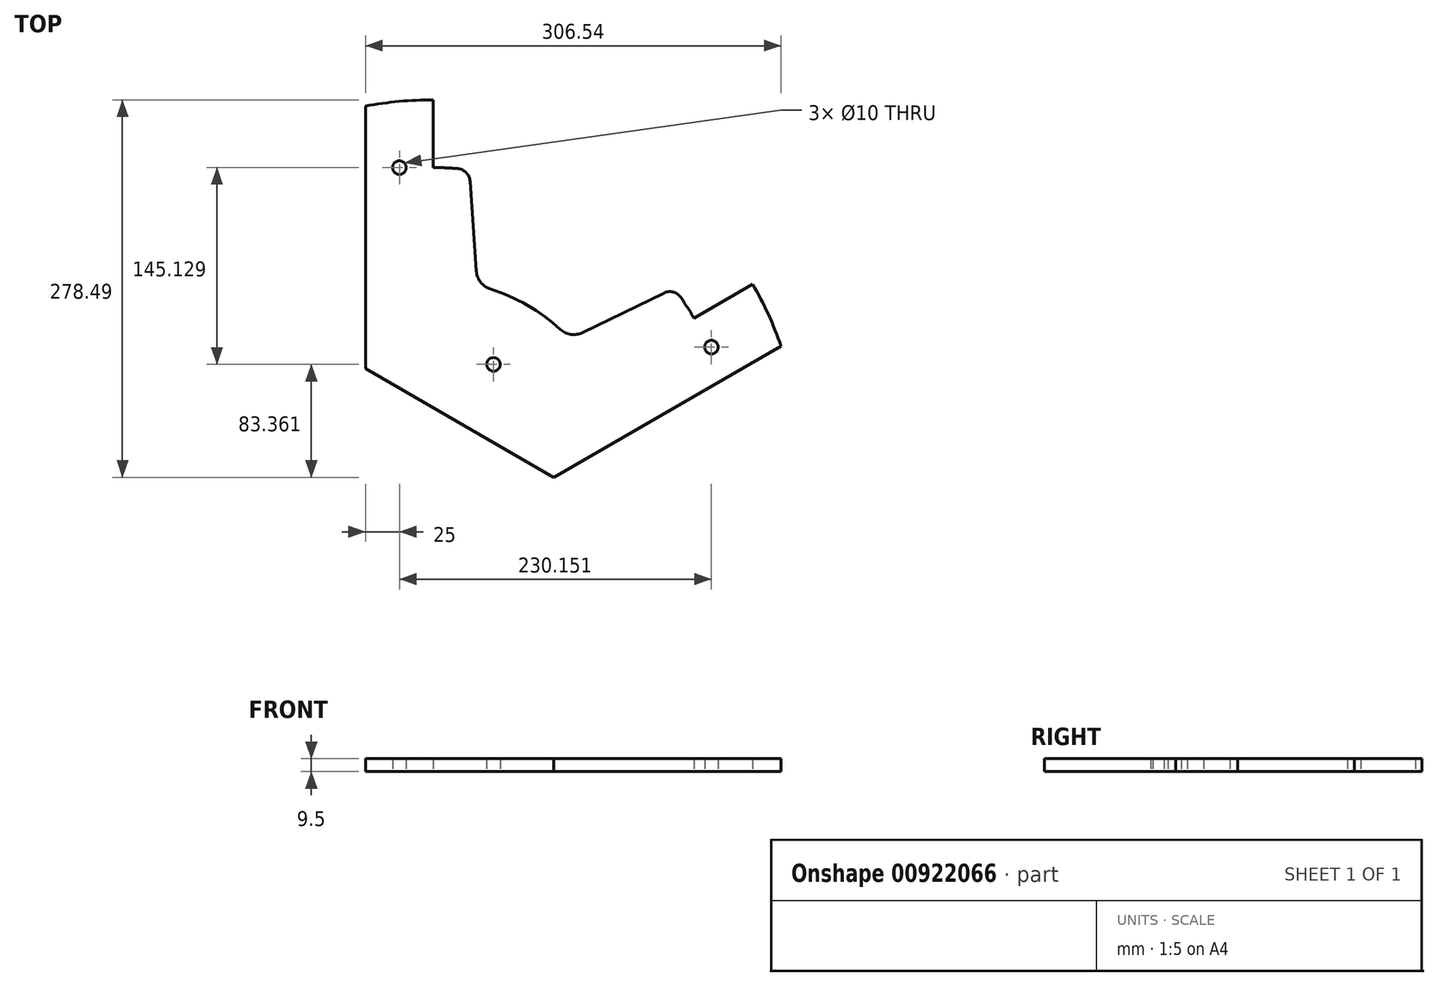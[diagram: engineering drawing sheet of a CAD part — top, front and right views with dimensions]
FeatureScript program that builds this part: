
annotation { "Feature Type Name" : "Feature", "Feature Type Description" : "" }
export const myFeature = defineFeature(function(context is Context, id is Id, definition is map)
    precondition{}
    {
        {
            var Q0;
            Q0=qCreatedBy(makeId("Top.planeOp"),FACE);
            var sketch = newSketch(context, id + "F0", { "sketchPlane" : qUnion([Q0])});
            skArc(sketch, "E0", {"start": v(17.92, 221.28) * mm, "mid": v(8.97, 221.82) * mm, "end": v(0, 222) * mm});
            skArc(sketch, "E1", {"start": v(256.54, 90.38) * mm, "mid": v(247.1, 113.68) * mm, "end": v(235.56, 136) * mm});
            skLineSegment(sketch, "E2", {"start": v(0, 222) * mm, "end": v(0, 272) * mm});
            skLineSegment(sketch, "E3", {"start": v(192.26, 111) * mm, "end": v(235.56, 136) * mm});
            skLineSegment(sketch, "E4", {"start": v(-50, 267.36) * mm, "end": v(-50, 73.63) * mm});
            skLineSegment(sketch, "E5", {"start": v(256.54, 90.38) * mm, "end": v(88.76, -6.49) * mm});
            skLineSegment(sketch, "E6", {"start": v(-50, 73.63) * mm, "end": v(88.76, -6.49) * mm});
            skPoint(sketch, "E7.orphan", {"position": v(-50, 0) * mm});
            skPoint(sketch, "E8", {"position": v(100.8, 95.72) * mm});
            skPoint(sketch, "E9", {"position": v(32.5, 135.15) * mm});
            skLineSegment(sketch, "E10", {"start": v(170.06, 129.47) * mm, "end": v(110.3, 100.35) * mm});
            skLineSegment(sketch, "E11", {"start": v(27.1, 212) * mm, "end": v(31.76, 145.69) * mm});
            skArc(sketch, "E12.trimOffspring", {"start": v(93.62, 102.75) * mm, "mid": v(69.5, 120.38) * mm, "end": v(42.17, 132.45) * mm});
            skArc(sketch, "E13.trimOffspring", {"start": v(192.26, 111) * mm, "mid": v(187.62, 118.68) * mm, "end": v(182.67, 126.16) * mm});
            skArc(sketch, "E14.trimOffspring", {"start": v(0, 272) * mm, "mid": v(-25.1, 270.84) * mm, "end": v(-50, 267.36) * mm});
            skCircle(sketch, "E15", {"center": v(-25, 222) * mm, "radius": 5 * mm});
            skCircle(sketch, "E16", {"center": v(205.15, 89.58) * mm, "radius": 5 * mm});
            skLineSegment(sketch, "E17", {"start": v(40.05, 79.37) * mm, "end": v(44.38, 76.87) * mm, "construction": true});
            skCircle(sketch, "E18", {"center": v(44.38, 76.87) * mm, "radius": 5 * mm});
            skPoint(sketch, "E19.orphan", {"position": v(138.76, 22.38) * mm});
            skPoint(sketch, "E20.visualSharp", {"position": v(26.5, 220.41) * mm});
            skArc(sketch, "E20.filletArc", {"start": v(27.1, 212) * mm, "mid": v(24.22, 218.34) * mm, "end": v(17.92, 221.28) * mm});
            skPoint(sketch, "E21.visualSharp", {"position": v(177.63, 133.16) * mm});
            skArc(sketch, "E21.filletArc", {"start": v(182.67, 126.16) * mm, "mid": v(176.98, 130.15) * mm, "end": v(170.06, 129.47) * mm});
            skArc(sketch, "E22.filletArc", {"start": v(31.76, 145.69) * mm, "mid": v(34.93, 137.47) * mm, "end": v(42.17, 132.45) * mm});
            skArc(sketch, "E23.filletArc", {"start": v(93.62, 102.75) * mm, "mid": v(101.59, 98.99) * mm, "end": v(110.3, 100.35) * mm});
            skSolve(sketch);
        }
        {
            var Q0;
            Q0 = qSketchRegion(id + "F0", true);
            extrude(context, id + "F1", {"entities" : qUnion([Q0]), "depth" : 9.5 * mm, "offsetDistance" : 25 * mm});
        }
    });
